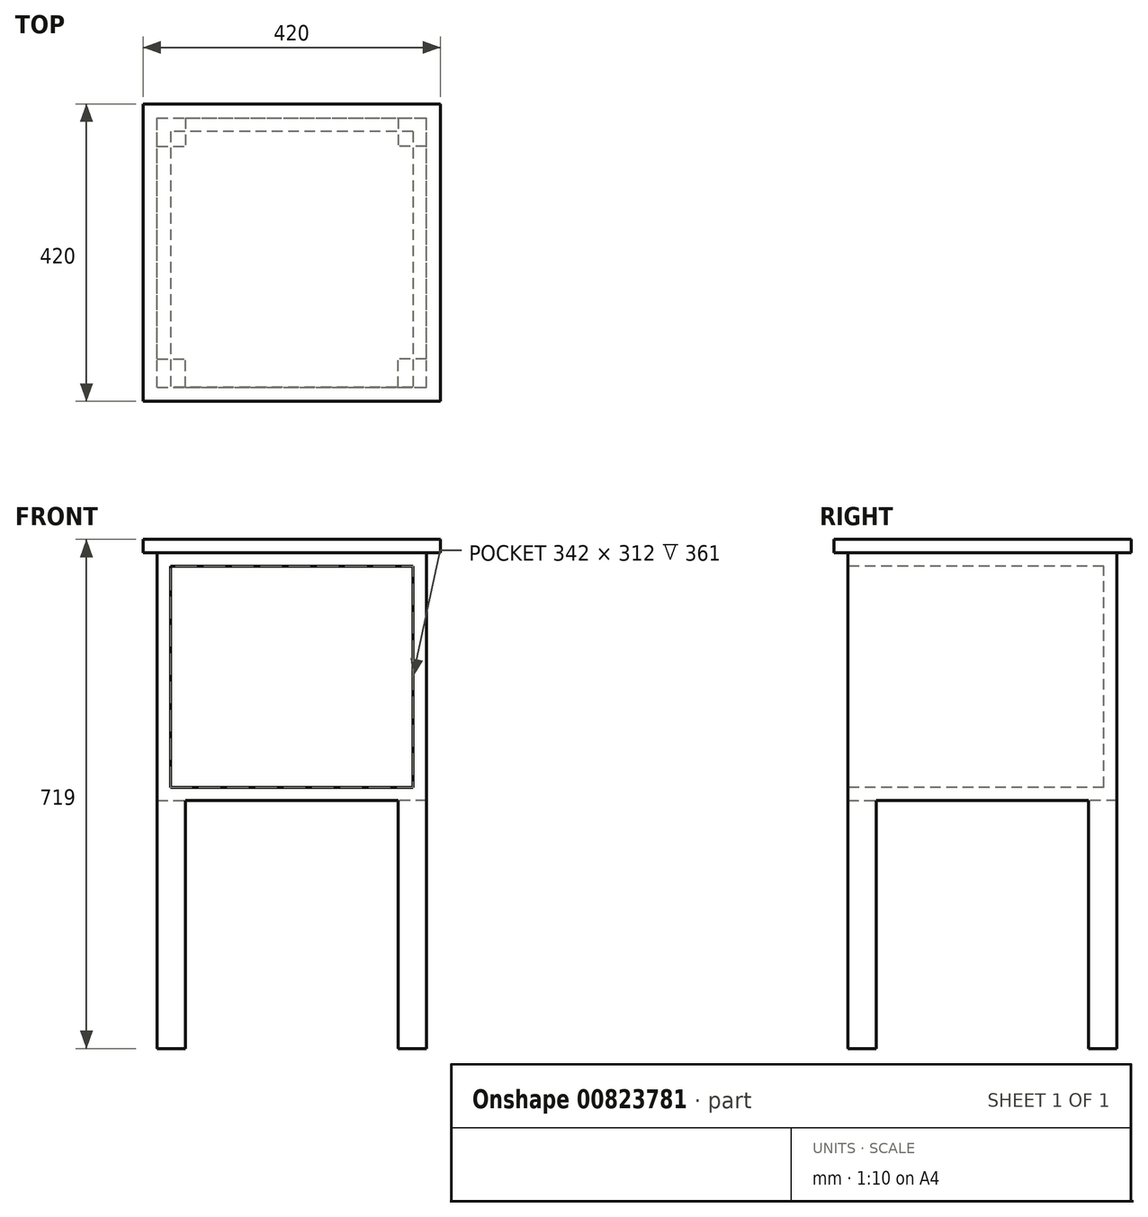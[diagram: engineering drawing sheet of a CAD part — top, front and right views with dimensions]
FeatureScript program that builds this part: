
annotation { "Feature Type Name" : "Feature", "Feature Type Description" : "" }
export const myFeature = defineFeature(function(context is Context, id is Id, definition is map)
    precondition{}
    {
        {
            var Q0;
            Q0=qCreatedBy(makeId("Top.planeOp"),FACE);
            var sketch = newSketch(context, id + "F0", { "sketchPlane" : qUnion([Q0])});
            skLineSegment(sketch, "E0.bottom", {"start": v(-190, -190) * mm, "end": v(190, -190) * mm});
            skLineSegment(sketch, "E0.top", {"start": v(-190, 190) * mm, "end": v(190, 190) * mm});
            skLineSegment(sketch, "E0.left", {"start": v(-190, -190) * mm, "end": v(-190, 190) * mm});
            skLineSegment(sketch, "E0.right", {"start": v(190, -190) * mm, "end": v(190, 190) * mm});
            skPoint(sketch, "E0.middle", {"position": v(0, 0) * mm});
            skSolve(sketch);
        }
        {
            var Q0;
            Q0=makeQuery(id+"F0.imprint","IMPRINT",FACE,{"disambiguationData":[TD([[makeQuery(id+"F0.imprint","IMPRINT",EDGE,{"derivedFrom":sQuery(id+"F0.wireOp",EDGE,"E0.bottom")}),1.0]])]});
            extrude(context, id + "F1", {"entities" : qUnion([Q0]), "depth" : 350 * mm, "offsetDistance" : 25 * mm});
        }
        {
            var Q0;
            Q0=makeQuery(id+"F1.opExtrude","SWEPT_FACE",FACE,{"disambiguationData":[OSD([sQuery(id+"F0.wireOp",EDGE,"E0.bottom")])]});
            var sketch = newSketch(context, id + "F2", { "sketchPlane" : qUnion([Q0])});
            skLineSegment(sketch, "E1.bottom", {"start": v(171, 19) * mm, "end": v(-171, 19) * mm});
            skLineSegment(sketch, "E1.top", {"start": v(171, 331) * mm, "end": v(-171, 331) * mm});
            skLineSegment(sketch, "E1.left", {"start": v(171, 19) * mm, "end": v(171, 331) * mm});
            skLineSegment(sketch, "E1.right", {"start": v(-171, 19) * mm, "end": v(-171, 331) * mm});
            skPoint(sketch, "E1.middle", {"position": v(0, 175) * mm});
            skPoint(sketch, "E1.middle.positionSnap0", {"position": v(190, 175) * mm});
            skPoint(sketch, "E1.centerSnap0", {"position": v(190, 175) * mm});
            skSolve(sketch);
        }
        {
            var Q0;
            Q0 = qSketchRegion(id + "F2", true);
            extrude(context, id + "F3", {"entities" : qUnion([Q0]), "operationType" : NewBodyOperationType.REMOVE, "oppositeDirection" : true, "depth" : 361 * mm, "offsetDistance" : 25 * mm});
        }
        {
            var Q0;
            Q0=makeQuery(id+"F1.opExtrude","CAP_FACE",FACE,{"disambiguationData":[OSD([sQuery(id+"F0.wireOp",EDGE,"E0.bottom"),sQuery(id+"F0.wireOp",EDGE,"E0.top"),sQuery(id+"F0.wireOp",EDGE,"E0.left"),sQuery(id+"F0.wireOp",EDGE,"E0.right")])],"isStart":true});
            var sketch = newSketch(context, id + "F4", { "sketchPlane" : qUnion([Q0])});
            skLineSegment(sketch, "E2.bottom", {"start": v(-190, 190) * mm, "end": v(-150, 190) * mm});
            skLineSegment(sketch, "E2.top", {"start": v(-190, 150) * mm, "end": v(-150, 150) * mm});
            skLineSegment(sketch, "E2.left", {"start": v(-190, 190) * mm, "end": v(-190, 150) * mm});
            skLineSegment(sketch, "E2.right", {"start": v(-150, 190) * mm, "end": v(-150, 150) * mm});
            skLineSegment(sketch, "E3.bottom", {"start": v(190, 190) * mm, "end": v(150, 190) * mm});
            skLineSegment(sketch, "E3.top", {"start": v(190, 150) * mm, "end": v(150, 150) * mm});
            skLineSegment(sketch, "E3.left", {"start": v(190, 190) * mm, "end": v(190, 150) * mm});
            skLineSegment(sketch, "E3.right", {"start": v(150, 190) * mm, "end": v(150, 150) * mm});
            skLineSegment(sketch, "E4.bottom", {"start": v(190, -190) * mm, "end": v(150, -190) * mm});
            skLineSegment(sketch, "E4.top", {"start": v(190, -150) * mm, "end": v(150, -150) * mm});
            skLineSegment(sketch, "E4.left", {"start": v(190, -190) * mm, "end": v(190, -150) * mm});
            skLineSegment(sketch, "E4.right", {"start": v(150, -190) * mm, "end": v(150, -150) * mm});
            skLineSegment(sketch, "E5.bottom", {"start": v(-190, -190) * mm, "end": v(-150, -190) * mm});
            skLineSegment(sketch, "E5.top", {"start": v(-190, -150) * mm, "end": v(-150, -150) * mm});
            skLineSegment(sketch, "E5.left", {"start": v(-190, -190) * mm, "end": v(-190, -150) * mm});
            skLineSegment(sketch, "E5.right", {"start": v(-150, -190) * mm, "end": v(-150, -150) * mm});
            skSolve(sketch);
        }
        {
            var Q0;
            Q0=makeQuery(id+"F4.imprint","IMPRINT",FACE,{"disambiguationData":[TD([[makeQuery(id+"F4.imprint","IMPRINT",EDGE,{"derivedFrom":sQuery(id+"F4.wireOp",EDGE,"E2.bottom")}),-1.0]])]});
            var Q1;
            Q1=makeQuery(id+"F4.imprint","IMPRINT",FACE,{"disambiguationData":[TD([[makeQuery(id+"F4.imprint","IMPRINT",EDGE,{"derivedFrom":sQuery(id+"F4.wireOp",EDGE,"E3.bottom")}),-1.0]])]});
            var Q2;
            Q2=makeQuery(id+"F4.imprint","IMPRINT",FACE,{"disambiguationData":[TD([[makeQuery(id+"F4.imprint","IMPRINT",EDGE,{"derivedFrom":sQuery(id+"F4.wireOp",EDGE,"E4.bottom")}),1.0]])]});
            var Q3;
            Q3=makeQuery(id+"F4.imprint","IMPRINT",FACE,{"disambiguationData":[TD([[makeQuery(id+"F4.imprint","IMPRINT",EDGE,{"derivedFrom":sQuery(id+"F4.wireOp",EDGE,"E5.bottom")}),1.0]])]});
            extrude(context, id + "F5", {"entities" : qUnion([Q0, Q1, Q2, Q3]), "operationType" : NewBodyOperationType.ADD, "depth" : 350 * mm, "offsetDistance" : 25 * mm});
        }
        {
            var Q0;
            Q0=makeQuery(id+"F1.opExtrude","CAP_FACE",FACE,{"disambiguationData":[OSD([sQuery(id+"F0.wireOp",EDGE,"E0.bottom"),sQuery(id+"F0.wireOp",EDGE,"E0.top"),sQuery(id+"F0.wireOp",EDGE,"E0.left"),sQuery(id+"F0.wireOp",EDGE,"E0.right")])],"isStart":false});
            var sketch = newSketch(context, id + "F6", { "sketchPlane" : qUnion([Q0])});
            skLineSegment(sketch, "E6.bottom", {"start": v(210, -210) * mm, "end": v(-210, -210) * mm});
            skLineSegment(sketch, "E6.top", {"start": v(210, 210) * mm, "end": v(-210, 210) * mm});
            skLineSegment(sketch, "E6.left", {"start": v(210, -210) * mm, "end": v(210, 210) * mm});
            skLineSegment(sketch, "E6.right", {"start": v(-210, -210) * mm, "end": v(-210, 210) * mm});
            skPoint(sketch, "E6.middle", {"position": v(0, 0) * mm});
            skSolve(sketch);
        }
        {
            var Q0;
            Q0 = qSketchRegion(id + "F6", true);
            extrude(context, id + "F7", {"entities" : qUnion([Q0]), "operationType" : NewBodyOperationType.ADD, "depth" : 19 * mm, "offsetDistance" : 25 * mm});
        }
    });
